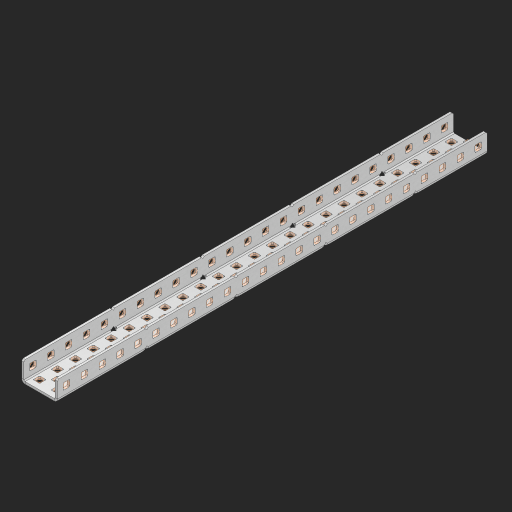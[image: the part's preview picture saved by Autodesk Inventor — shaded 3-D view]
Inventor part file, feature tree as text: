
AUTODESK INVENTOR PART (.ipt)
format: ipt  version: 2023 (Build 270158000, 158)  size: 1,592,320 bytes
history: native  units: in
note: dims shown in document units (in); Inventor stores cm internally (conversion verified against a paired STEP export)
features: other x127, extrude x118, sheet_metal_op x11, sketch x10, pattern_linear x2, mirror x1, chamfer x1
ambient origin geometry x8: Origin, YZ Plane, XZ Plane, XY Plane, X Axis, Y Axis, Z Axis, Center Point
bodies: Solid1 (feature_tree), Body (feature_tree)
feature tree (270):
  sheet_metal_op  "Flanges"
  other  "Flange Pattern Plane"
  other  "Flange Pattern Sketch"
  sheet_metal_op  "Flange Pattern"
  sheet_metal_op  "Body Pattern"
  pattern_linear  "Center Pattern"  Spacing1=0.0625in  [1 undecoded]
  other  "Arc Length"
  mirror  "Notch Mirror"
  pattern_linear  "Notch Pattern"  Spacing1=0.182in  [1 undecoded]
  chamfer  "End Chamfer"
  extrude  "Half Cut"  Depth=0.02in
  sketch  "Sketch1"  dims[d0=1.0in]
  other  "Plate1"
  sketch  "Sketch2"  dims[d1=12.0in]
  other  "Plate2"
  sheet_metal_op  "Bend1"
  sheet_metal_op  "Corner1"
  sketch  "Sketch3"  dims[d2=0.0625in]
  sketch  "Sketch7"  dims[d3=0.0625in]
  other  "Srf1"
  other  "Srf2"
  sketch  "Sketch8"  dims[d4=0.0312in]
  sketch  "Sketch9"  dims[d5=0.125in]
  other  "Srf91"
  sheet_metal_op  "Body Pattern Sketch"
  other  "Srf92"
  sketch  "Sketch13"  dims[d6=0.0625in]
  sketch  "Sketch14"  dims[d7=0.5in d8=90.0deg d9=0.0312in]
  sketch  "Sketch15"  dims[d10=0.25in]
  sketch  "Sketch16"  dims[d11=0.0625in d12=0.0625in d16=0.182in d17=0.02in d18=0.0625in d19=0.0in d20=0.25in d21=0.25in d38=9.4488in d40=0.5in d41=0.7874in d43=1.0in d46=0.172in d47=1.0in d48=0.0in d49=0.182in d50=0.02in d51=0.25in d52=0.25in d53=0.0625in d54=0.0in d55=0.172in d56=1.0in d57=0.0in d58=0.25in d60=9.4488in d62=0.5in d63=0.7874in d65=0.5in d85=0.1473in d86=0.1782in d88=0.04in d89=0.0625in d90=0.0in d91=0.04in d92=0.0491in d95=2.5in d96=0.04in d97=0.25in d98=45.0deg d99=0.25in d100=0.5in d101=0.0in d102=2.497in d106=0.182in d107=0.02in d108=0.5in d109=0.5in d110=0.0625in d111=0.0in d112=0.172in d113=0.5in d114=0.0in d117=0.5in d118=0.5in d119=0.5in]
  other  "Srf786"
  other  "Srf823"
  other  "Srf824"
  other  "Srf825"
  other  "Srf826"
  other  "Srf827"
  other  "Srf828"
  other  "Srf829"
  other  "Srf856"
  other  "Srf857"
  other  "Srf858"
  other  "Srf859"
  other  "Srf860"
  other  "Srf861"
  other  "Srf862"
  other  "Srf889"
  other  "Srf890"
  other  "Srf891"
  other  "Srf892"
  other  "Srf893"
  other  "Srf894"
  other  "Srf895"
  other  "Srf896"
  other  "Srf922"
  other  "Srf923"
  other  "Srf924"
  other  "Srf925"
  other  "Srf926"
  other  "Srf959"
  other  "Srf960"
  other  "Srf961"
  other  "Srf962"
  other  "Srf963"
  other  "Srf996"
  other  "Srf997"
  other  "Srf998"
  other  "Srf999"
  other  "Srf1000"
  other  "Srf1143"
  other  "Srf1144"
  other  "Srf1145"
  other  "Srf1146"
  other  "Srf1147"
  other  "Srf1148"
  other  "Srf1149"
  other  "Srf1150"
  other  "Srf1151"
  other  "Srf1152"
  other  "Srf1153"
  other  "Srf1154"
  other  "Srf1155"
  other  "Srf1156"
  other  "Srf1157"
  other  "Srf1158"
  other  "Srf1159"
  other  "Srf1160"
  other  "Srf1161"
  other  "Srf1162"
  other  "Srf1163"
  other  "Srf1164"
  other  "Srf1165"
  other  "Srf1166"
  other  "Srf1167"
  other  "Srf1168"
  other  "Srf1169"
  other  "Srf1170"
  other  "Srf1171"
  other  "Srf1172"
  other  "Srf1173"
  other  "Srf1174"
  other  "Srf1175"
  other  "Srf1176"
  other  "Srf1199"
  other  "Srf1200"
  other  "Srf1201"
  other  "Srf1202"
  other  "Srf1203"
  other  "Srf1204"
  other  "Srf1205"
  other  "Srf1206"
  other  "Srf1207"
  other  "Srf1208"
  other  "Srf1209"
  other  "Srf1210"
  other  "Srf1211"
  other  "Srf1212"
  other  "Srf1213"
  other  "Srf1214"
  other  "Srf1215"
  other  "Srf1216"
  other  "Srf1217"
  other  "Srf1218"
  other  "Srf1219"
  other  "Srf1220"
  other  "Srf1221"
  other  "Srf1222"
  other  "Srf1223"
  other  "Srf1224"
  other  "Srf1225"
  other  "Srf1226"
  other  "Srf1227"
  other  "Srf1228"
  other  "Srf1229"
  other  "Srf1230"
  other  "Srf1231"
  other  "Srf1232"
  other  "Srf1255"
  other  "Srf1256"
  other  "Srf1257"
  other  "Srf1258"
  other  "Srf1259"
  other  "Srf1260"
  other  "Srf1261"
  other  "Srf1262"
  other  "Srf1263"
  other  "Srf1264"
  sheet_metal_op  "Flange Stamp"
  sheet_metal_op  "Flange Circle"
  sheet_metal_op  "Body Stamp"
  sheet_metal_op  "Body Circle"
  other  "Center Stamp"
  other  "Center Circle"
  sheet_metal_op  "Notch"
  extrude  "ExtrusionSrf2"  Depth=0.0625in
  extrude  "ExtrusionSrf92"  TaperAngle=0.0deg  [1 undecoded]
  extrude  "ExtrusionSrf823"  Depth=0.5in
  extrude  "ExtrusionSrf824"  Depth=0.5in
  extrude  "ExtrusionSrf825"  Depth=0.5in
  extrude  "ExtrusionSrf826"  Depth=0.5in
  extrude  "ExtrusionSrf827"  Depth=1.0in TaperAngle=0.0deg
  extrude  "ExtrusionSrf828"  Depth=0.5in
  extrude  "ExtrusionSrf829"  Depth=0.02in
  extrude  "ExtrusionSrf856"  Depth=0.5in
  extrude  "ExtrusionSrf857"  Depth=0.5in
  extrude  "ExtrusionSrf858"  Depth=0.0625in
  extrude  "ExtrusionSrf859"  TaperAngle=0.0deg  [1 undecoded]
  extrude  "ExtrusionSrf860"  Depth=0.5in
  extrude  "ExtrusionSrf861"  Depth=1.0in TaperAngle=0.0deg
  extrude  "ExtrusionSrf862"  Depth=0.5in
  extrude  "ExtrusionSrf889"  Depth=0.5in
  extrude  "ExtrusionSrf890"  Depth=0.5in
  extrude  "ExtrusionSrf891"  Depth=0.5in
  extrude  "ExtrusionSrf892"  Depth=0.5in
  extrude  "ExtrusionSrf893"  Depth=0.5in
  extrude  "ExtrusionSrf894"  Depth=0.0625in
  extrude  "ExtrusionSrf895"  TaperAngle=0.0deg  [1 undecoded]
  extrude  "ExtrusionSrf896"  Depth=0.5in
  extrude  "ExtrusionSrf922"  Depth=0.5in
  extrude  "ExtrusionSrf923"  Depth=2.5in
  extrude  "ExtrusionSrf924"  Depth=0.5in TaperAngle=45.0deg
  extrude  "ExtrusionSrf925"  Depth=0.5in
  extrude  "ExtrusionSrf926"  Depth=0.5in TaperAngle=0.0deg
  extrude  "ExtrusionSrf959"  Depth=0.5in
  extrude  "ExtrusionSrf960"  Depth=0.5in
  extrude  "ExtrusionSrf961"  Depth=0.02in
  extrude  "ExtrusionSrf962"  Depth=0.5in
  extrude  "ExtrusionSrf963"  Depth=0.5in
  extrude  "ExtrusionSrf996"  Depth=0.0625in
  extrude  "ExtrusionSrf997"  TaperAngle=0.0deg  [1 undecoded]
  extrude  "ExtrusionSrf998"  Depth=0.5in
  extrude  "ExtrusionSrf999"  Depth=0.5in TaperAngle=0.0deg
  extrude  "ExtrusionSrf1000"  Depth=0.5in
  extrude  "ExtrusionSrf1143"  Depth=0.5in
  extrude  "ExtrusionSrf1144"  Depth=0.5in
  extrude  "ExtrusionSrf1145"  [1 undecoded]
  extrude  "ExtrusionSrf1146"  [1 undecoded]
  extrude  "ExtrusionSrf1147"  [1 undecoded]
  extrude  "ExtrusionSrf1148"  [1 undecoded]
  extrude  "ExtrusionSrf1149"  [1 undecoded]
  extrude  "ExtrusionSrf1150"  [1 undecoded]
  extrude  "ExtrusionSrf1151"  [1 undecoded]
  extrude  "ExtrusionSrf1152"  [1 undecoded]
  extrude  "ExtrusionSrf1153"  [1 undecoded]
  extrude  "ExtrusionSrf1154"  [1 undecoded]
  extrude  "ExtrusionSrf1155"  [1 undecoded]
  extrude  "ExtrusionSrf1156"  [1 undecoded]
  extrude  "ExtrusionSrf1157"  [1 undecoded]
  extrude  "ExtrusionSrf1158"  [1 undecoded]
  extrude  "ExtrusionSrf1159"  [1 undecoded]
  extrude  "ExtrusionSrf1160"  [1 undecoded]
  extrude  "ExtrusionSrf1161"  [1 undecoded]
  extrude  "ExtrusionSrf1162"  [1 undecoded]
  extrude  "ExtrusionSrf1163"  [1 undecoded]
  extrude  "ExtrusionSrf1164"  [1 undecoded]
  extrude  "ExtrusionSrf1165"  [1 undecoded]
  extrude  "ExtrusionSrf1166"  [1 undecoded]
  extrude  "ExtrusionSrf1167"  [1 undecoded]
  extrude  "ExtrusionSrf1168"  [1 undecoded]
  extrude  "ExtrusionSrf1169"  [1 undecoded]
  extrude  "ExtrusionSrf1170"  [1 undecoded]
  extrude  "ExtrusionSrf1171"  [1 undecoded]
  extrude  "ExtrusionSrf1172"  [1 undecoded]
  extrude  "ExtrusionSrf1173"  [1 undecoded]
  extrude  "ExtrusionSrf1174"  [1 undecoded]
  extrude  "ExtrusionSrf1175"  [1 undecoded]
  extrude  "ExtrusionSrf1176"  [1 undecoded]
  extrude  "ExtrusionSrf1199"  [1 undecoded]
  extrude  "ExtrusionSrf1200"  [1 undecoded]
  extrude  "ExtrusionSrf1201"  [1 undecoded]
  extrude  "ExtrusionSrf1202"  [1 undecoded]
  extrude  "ExtrusionSrf1203"  [1 undecoded]
  extrude  "ExtrusionSrf1204"  [1 undecoded]
  extrude  "ExtrusionSrf1205"  [1 undecoded]
  extrude  "ExtrusionSrf1206"  [1 undecoded]
  extrude  "ExtrusionSrf1207"  [1 undecoded]
  extrude  "ExtrusionSrf1208"  [1 undecoded]
  extrude  "ExtrusionSrf1209"  [1 undecoded]
  extrude  "ExtrusionSrf1210"  [1 undecoded]
  extrude  "ExtrusionSrf1211"  [1 undecoded]
  extrude  "ExtrusionSrf1212"  [1 undecoded]
  extrude  "ExtrusionSrf1213"  [1 undecoded]
  extrude  "ExtrusionSrf1214"  [1 undecoded]
  extrude  "ExtrusionSrf1215"  [1 undecoded]
  extrude  "ExtrusionSrf1216"  [1 undecoded]
  extrude  "ExtrusionSrf1217"  [1 undecoded]
  extrude  "ExtrusionSrf1218"  [1 undecoded]
  extrude  "ExtrusionSrf1219"  [1 undecoded]
  extrude  "ExtrusionSrf1220"  [1 undecoded]
  extrude  "ExtrusionSrf1221"  [1 undecoded]
  extrude  "ExtrusionSrf1222"  [1 undecoded]
  extrude  "ExtrusionSrf1223"  [1 undecoded]
  extrude  "ExtrusionSrf1224"  [1 undecoded]
  extrude  "ExtrusionSrf1225"  [1 undecoded]
  extrude  "ExtrusionSrf1226"  [1 undecoded]
  extrude  "ExtrusionSrf1227"  [1 undecoded]
  extrude  "ExtrusionSrf1228"  [1 undecoded]
  extrude  "ExtrusionSrf1229"  [1 undecoded]
  extrude  "ExtrusionSrf1230"  [1 undecoded]
  extrude  "ExtrusionSrf1231"  [1 undecoded]
  extrude  "ExtrusionSrf1232"  [1 undecoded]
  extrude  "ExtrusionSrf1255"  [1 undecoded]
  extrude  "ExtrusionSrf1256"  [1 undecoded]
  extrude  "ExtrusionSrf1257"  [1 undecoded]
  extrude  "ExtrusionSrf1258"  [1 undecoded]
  extrude  "ExtrusionSrf1259"  [1 undecoded]
  extrude  "ExtrusionSrf1260"  [1 undecoded]
  extrude  "ExtrusionSrf1261"  [1 undecoded]
  extrude  "ExtrusionSrf1262"  [1 undecoded]
  extrude  "ExtrusionSrf1263"  [1 undecoded]
  extrude  "ExtrusionSrf1264"  [1 undecoded]
note: 82 required parameter values undecoded (feature->parameter linkage not recoverable at this tier; creation-order binding heuristic only, values carry confidence <= 0.55)
